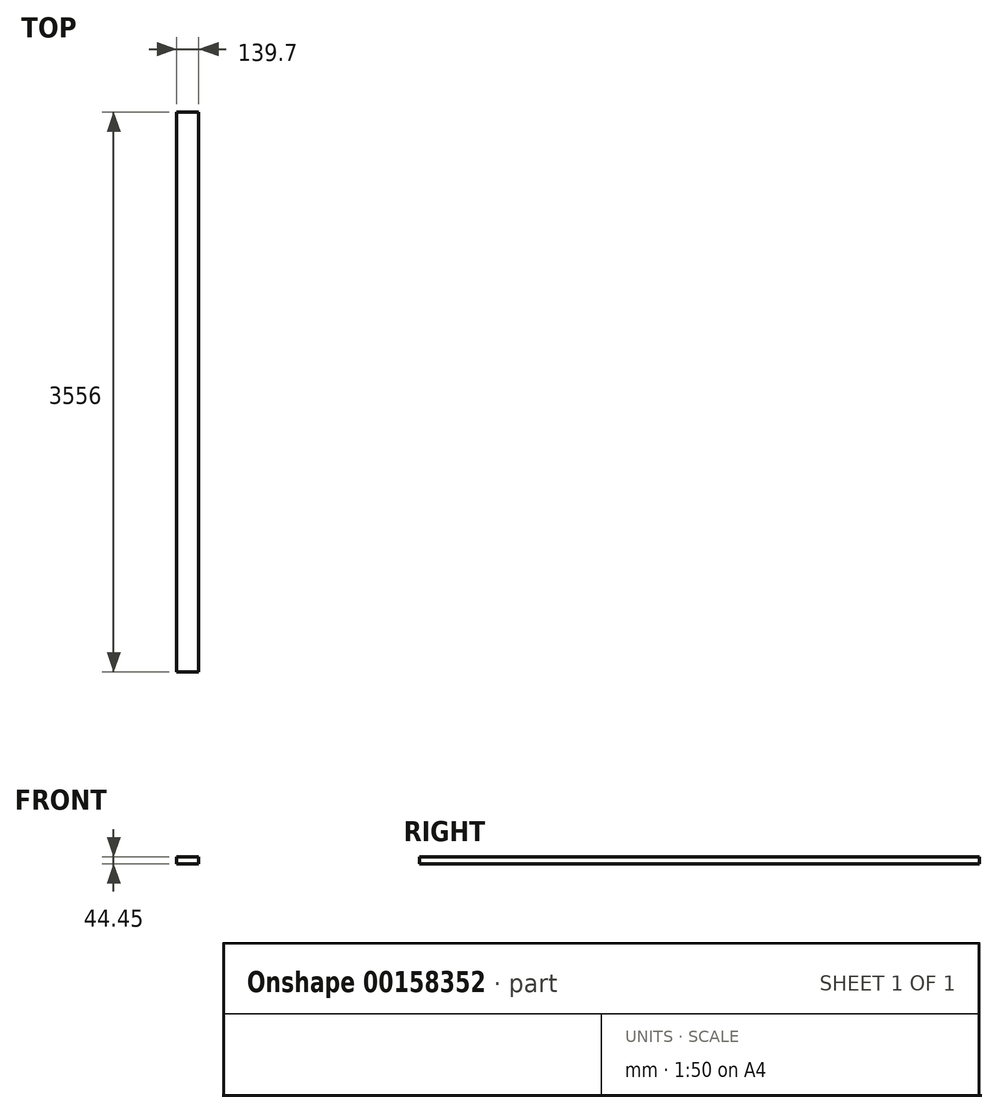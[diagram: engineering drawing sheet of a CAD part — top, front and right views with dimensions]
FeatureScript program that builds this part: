
annotation { "Feature Type Name" : "Feature", "Feature Type Description" : "" }
export const myFeature = defineFeature(function(context is Context, id is Id, definition is map)
    precondition{}
    {
        {
            var Q0;
            Q0=qCreatedBy(makeId("Front.planeOp"),FACE);
            var sketch = newSketch(context, id + "F0", { "sketchPlane" : qUnion([Q0])});
            skLineSegment(sketch, "E0.bottom", {"start": v(-101.95, 39.06) * mm, "end": v(37.75, 39.06) * mm});
            skLineSegment(sketch, "E0.top", {"start": v(-101.95, -5.39) * mm, "end": v(37.75, -5.39) * mm});
            skLineSegment(sketch, "E0.left", {"start": v(-101.95, 39.06) * mm, "end": v(-101.95, -5.39) * mm});
            skLineSegment(sketch, "E0.right", {"start": v(37.75, 39.06) * mm, "end": v(37.75, -5.39) * mm});
            skSolve(sketch);
        }
        {
            var Q0;
            Q0=makeQuery(id+"F0.imprint","IMPRINT",FACE,{"disambiguationData":[TD([[makeQuery(id+"F0.imprint","IMPRINT",EDGE,{"derivedFrom":sQuery(id+"F0.wireOp",EDGE,"E0.bottom")}),-1.0]])]});
            extrude(context, id + "F1", {"entities" : qUnion([Q0]), "endBound" : BoundingType.SYMMETRIC, "depth" : 3556 * mm});
        }
    });
